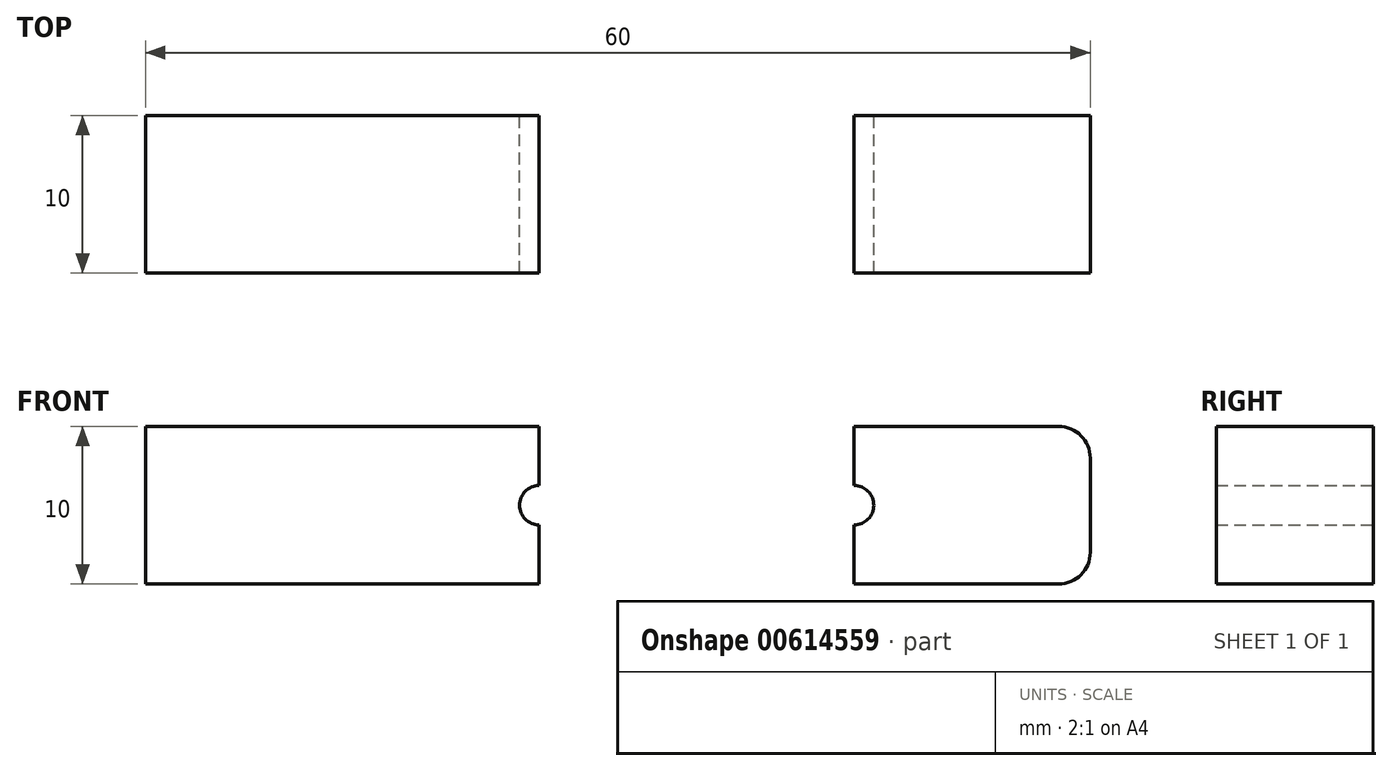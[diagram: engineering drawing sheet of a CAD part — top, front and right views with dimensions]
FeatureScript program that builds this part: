
annotation { "Feature Type Name" : "Feature", "Feature Type Description" : "" }
export const myFeature = defineFeature(function(context is Context, id is Id, definition is map)
    precondition{}
    {
        {
            var Q0;
            Q0=qCreatedBy(makeId("Front.planeOp"),FACE);
            var sketch = newSketch(context, id + "F0", { "sketchPlane" : qUnion([Q0])});
            skLineSegment(sketch, "E0.bottom", {"start": v(-26.48, 23.05) * mm, "end": v(31.52, 23.05) * mm});
            skLineSegment(sketch, "E0.top", {"start": v(-26.48, 13.05) * mm, "end": v(33.52, 13.05) * mm});
            skLineSegment(sketch, "E0.left", {"start": v(-26.48, 23.05) * mm, "end": v(-26.48, 13.05) * mm});
            skLineSegment(sketch, "E0.right", {"start": v(33.52, 21.05) * mm, "end": v(33.52, 15.05) * mm});
            skLineSegment(sketch, "E1", {"start": v(31.52, 13.05) * mm, "end": v(18.52, 13.05) * mm});
            skLineSegment(sketch, "E2", {"start": v(18.52, 13.05) * mm, "end": v(-1.48, 13.05) * mm});
            skLineSegment(sketch, "E3", {"start": v(18.52, 13.05) * mm, "end": v(18.52, 23.05) * mm});
            skLineSegment(sketch, "E4", {"start": v(-1.48, 13.05) * mm, "end": v(-1.48, 23.05) * mm});
            skCircle(sketch, "E5", {"center": v(18.52, 18.05) * mm, "radius": 1.25 * mm});
            skCircle(sketch, "E6", {"center": v(-1.48, 18.05) * mm, "radius": 1.25 * mm});
            skPoint(sketch, "E7.visualSharp", {"position": v(33.52, 23.05) * mm});
            skArc(sketch, "E7.filletArc", {"start": v(33.52, 21.05) * mm, "mid": v(32.94, 22.46) * mm, "end": v(31.52, 23.05) * mm});
            skPoint(sketch, "E8.visualSharp", {"position": v(33.52, 13.05) * mm});
            skArc(sketch, "E8.filletArc", {"start": v(31.52, 13.05) * mm, "mid": v(32.94, 13.64) * mm, "end": v(33.52, 15.05) * mm});
            skSolve(sketch);
        }
        {
            var Q0;
            {var subQ5=sQuery(id+"F0.wireOp",EDGE,"E0.left");Q0=makeQuery(id+"F0.imprint","IMPRINT",FACE,{"disambiguationData":[TD([[makeQuery(id+"F0.imprint","IMPRINT",EDGE,{"derivedFrom":subQ5}),1.0]])]});}
            var Q1;
            {var subQ5=sQuery(id+"F0.wireOp",EDGE,"E2");Q1=makeQuery(id+"F0.imprint","IMPRINT",FACE,{"disambiguationData":[TD([[makeQuery(id+"F0.imprint","IMPRINT",EDGE,{"derivedFrom":subQ5}),-1.0]])]});}
            var Q2;
            Q2=makeQuery(id+"F0.imprint","IMPRINT",FACE,{"disambiguationData":[TD([[makeQuery(id+"F0.imprint","IMPRINT",EDGE,{"derivedFrom":sQuery(id+"F0.wireOp",EDGE,"E0.right")}),-1.0]])]});
            extrude(context, id + "F1", {"entities" : qUnion([Q0, Q1, Q2]), "depth" : 10 * mm, "offsetDistance" : 25 * mm});
        }
    });
